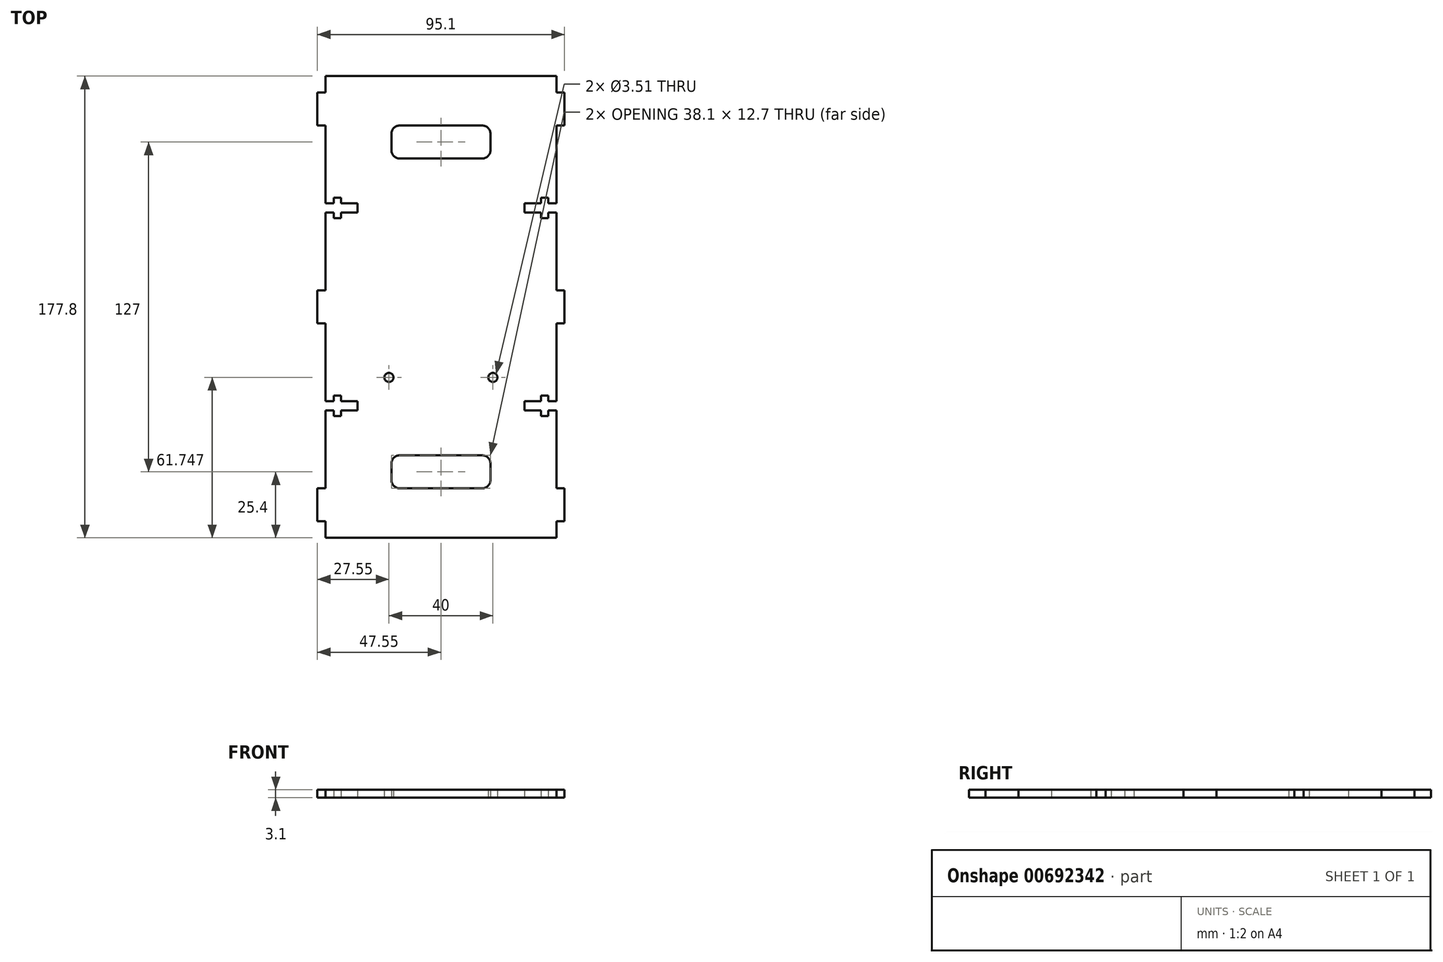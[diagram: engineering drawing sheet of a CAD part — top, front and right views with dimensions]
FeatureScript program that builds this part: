
annotation { "Feature Type Name" : "Feature", "Feature Type Description" : "" }
export const myFeature = defineFeature(function(context is Context, id is Id, definition is map)
    precondition{}
    {
        {
            var Q0;
            Q0=qCreatedBy(makeId("Top.planeOp"),FACE);
            var sketch = newSketch(context, id + "F0", { "sketchPlane" : qUnion([Q0])});
            skLineSegment(sketch, "E0.bottom", {"start": v(-44.45, 88.9) * mm, "end": v(44.45, 88.9) * mm});
            skLineSegment(sketch, "E0.top", {"start": v(-44.45, -88.9) * mm, "end": v(44.45, -88.9) * mm});
            skLineSegment(sketch, "E0.left", {"start": v(-44.45, 88.9) * mm, "end": v(-44.45, 82.55) * mm});
            skLineSegment(sketch, "E0.right", {"start": v(44.45, 88.9) * mm, "end": v(44.45, 82.55) * mm});
            skPoint(sketch, "E0.middle", {"position": v(0, 0) * mm});
            skCircle(sketch, "E1", {"center": v(-20, -27.15) * mm, "radius": 1.75 * mm});
            skCircle(sketch, "E2.MirrorC", {"center": v(20, -27.15) * mm, "radius": 1.75 * mm});
            skLineSegment(sketch, "E3", {"start": v(-44.45, 38.1) * mm, "end": v(44.45, 38.1) * mm, "construction": true});
            skLineSegment(sketch, "E4.bottom", {"start": v(-44.45, 39.85) * mm, "end": v(-41.27, 39.85) * mm});
            skLineSegment(sketch, "E4.top", {"start": v(-44.45, 36.35) * mm, "end": v(-41.27, 36.35) * mm});
            skPoint(sketch, "E4.middle", {"position": v(-42.86, 38.1) * mm});
            skLineSegment(sketch, "E5.bottom", {"start": v(-41.27, 42.07) * mm, "end": v(-38.5, 42.07) * mm});
            skLineSegment(sketch, "E5.top", {"start": v(-41.27, 34.13) * mm, "end": v(-38.5, 34.13) * mm});
            skLineSegment(sketch, "E5.left", {"start": v(-41.28, 42.07) * mm, "end": v(-41.28, 39.85) * mm});
            skLineSegment(sketch, "E5.right", {"start": v(-38.5, 42.07) * mm, "end": v(-38.5, 39.85) * mm});
            skPoint(sketch, "E5.middle", {"position": v(-39.89, 38.1) * mm});
            skLineSegment(sketch, "E6.bottom", {"start": v(-38.5, 39.85) * mm, "end": v(-32.15, 39.85) * mm});
            skLineSegment(sketch, "E6.top", {"start": v(-38.5, 36.35) * mm, "end": v(-32.15, 36.35) * mm});
            skLineSegment(sketch, "E6.right", {"start": v(-32.15, 39.85) * mm, "end": v(-32.15, 36.35) * mm});
            skPoint(sketch, "E6.middle", {"position": v(-35.32, 38.1) * mm});
            skLineSegment(sketch, "E7.trimOffspring", {"start": v(-41.28, 36.35) * mm, "end": v(-41.28, 34.13) * mm});
            skLineSegment(sketch, "E8.trimOffspring", {"start": v(-38.5, 36.35) * mm, "end": v(-38.5, 34.13) * mm});
            skLineSegment(sketch, "E9.trimOffspring", {"start": v(-44.45, 36.35) * mm, "end": v(-44.45, 6.35) * mm});
            skLineSegment(sketch, "E10.MirrorCS", {"start": v(-38.5, -36.35) * mm, "end": v(-38.5, -34.13) * mm});
            skLineSegment(sketch, "E11.MirrorCS", {"start": v(-38.5, -39.85) * mm, "end": v(-32.15, -39.85) * mm});
            skLineSegment(sketch, "E12.MirrorCS", {"start": v(-41.27, -36.35) * mm, "end": v(-41.27, -34.13) * mm});
            skLineSegment(sketch, "E13.MirrorCS", {"start": v(-38.5, -42.07) * mm, "end": v(-38.5, -39.85) * mm});
            skLineSegment(sketch, "E14.MirrorCS", {"start": v(-41.27, -42.07) * mm, "end": v(-41.27, -39.85) * mm});
            skLineSegment(sketch, "E15.MirrorCS", {"start": v(-41.27, -34.13) * mm, "end": v(-38.5, -34.13) * mm});
            skLineSegment(sketch, "E16.MirrorCS", {"start": v(-41.27, -42.07) * mm, "end": v(-38.5, -42.07) * mm});
            skLineSegment(sketch, "E17.MirrorCS", {"start": v(-44.45, -39.85) * mm, "end": v(-41.27, -39.85) * mm});
            skLineSegment(sketch, "E18.MirrorCS", {"start": v(-44.45, -36.35) * mm, "end": v(-41.27, -36.35) * mm});
            skPoint(sketch, "E19.MirrorP", {"position": v(-42.86, -38.1) * mm});
            skLineSegment(sketch, "E20.MirrorCS", {"start": v(-44.45, -36.35) * mm, "end": v(-44.45, -6.35) * mm});
            skPoint(sketch, "E21.MirrorP", {"position": v(-35.32, -38.1) * mm});
            skLineSegment(sketch, "E22.MirrorCS", {"start": v(-38.5, -36.35) * mm, "end": v(-32.15, -36.35) * mm});
            skLineSegment(sketch, "E23.MirrorCS", {"start": v(-32.15, -39.85) * mm, "end": v(-32.15, -36.35) * mm});
            skPoint(sketch, "E24.MirrorP", {"position": v(-39.89, -38.1) * mm});
            skLineSegment(sketch, "E25.MirrorCS", {"start": v(-44.45, -88.9) * mm, "end": v(-44.45, -82.55) * mm});
            skLineSegment(sketch, "E26.MirrorCS", {"start": v(-44.45, -38.1) * mm, "end": v(44.45, -38.1) * mm, "construction": true});
            skLineSegment(sketch, "E27.trimOffspring", {"start": v(-44.45, -39.85) * mm, "end": v(-44.45, -69.85) * mm});
            skLineSegment(sketch, "E28.trimOffspring", {"start": v(-44.45, 39.85) * mm, "end": v(-44.45, 69.85) * mm});
            skLineSegment(sketch, "E29.MirrorCS", {"start": v(44.45, 36.35) * mm, "end": v(41.27, 36.35) * mm});
            skLineSegment(sketch, "E30.MirrorCS", {"start": v(44.45, 39.85) * mm, "end": v(41.27, 39.85) * mm});
            skLineSegment(sketch, "E31.MirrorCS", {"start": v(38.5, 36.35) * mm, "end": v(38.5, 34.13) * mm});
            skPoint(sketch, "E32.MirrorP", {"position": v(42.86, 38.1) * mm});
            skLineSegment(sketch, "E33.MirrorCS", {"start": v(44.45, -39.85) * mm, "end": v(41.27, -39.85) * mm});
            skLineSegment(sketch, "E34.MirrorCS", {"start": v(44.45, -36.35) * mm, "end": v(41.27, -36.35) * mm});
            skLineSegment(sketch, "E35.MirrorCS", {"start": v(38.5, 42.07) * mm, "end": v(38.5, 39.85) * mm});
            skLineSegment(sketch, "E36.MirrorCS", {"start": v(41.27, 42.07) * mm, "end": v(41.27, 39.85) * mm});
            skLineSegment(sketch, "E37.MirrorCS", {"start": v(41.27, 34.13) * mm, "end": v(38.5, 34.13) * mm});
            skLineSegment(sketch, "E38.MirrorCS", {"start": v(41.27, 36.35) * mm, "end": v(41.27, 34.13) * mm});
            skLineSegment(sketch, "E39.MirrorCS", {"start": v(41.27, 42.07) * mm, "end": v(38.5, 42.07) * mm});
            skLineSegment(sketch, "E40.MirrorCS", {"start": v(38.5, -42.07) * mm, "end": v(38.5, -39.85) * mm});
            skLineSegment(sketch, "E41.MirrorCS", {"start": v(41.27, -42.07) * mm, "end": v(38.5, -42.07) * mm});
            skPoint(sketch, "E42.MirrorP", {"position": v(39.89, 38.1) * mm});
            skPoint(sketch, "E43.MirrorP", {"position": v(42.86, -38.1) * mm});
            skLineSegment(sketch, "E44.MirrorCS", {"start": v(32.15, -39.85) * mm, "end": v(32.15, -36.35) * mm});
            skLineSegment(sketch, "E45.MirrorCS", {"start": v(41.27, -36.35) * mm, "end": v(41.27, -34.13) * mm});
            skLineSegment(sketch, "E46.MirrorCS", {"start": v(41.27, -34.13) * mm, "end": v(38.5, -34.13) * mm});
            skLineSegment(sketch, "E47.MirrorCS", {"start": v(32.15, 39.85) * mm, "end": v(32.15, 36.35) * mm});
            skLineSegment(sketch, "E48.MirrorCS", {"start": v(41.27, -42.07) * mm, "end": v(41.27, -39.85) * mm});
            skPoint(sketch, "E49.MirrorP", {"position": v(39.89, -38.1) * mm});
            skLineSegment(sketch, "E50.MirrorCS", {"start": v(38.5, -36.35) * mm, "end": v(38.5, -34.13) * mm});
            skLineSegment(sketch, "E51.MirrorCS", {"start": v(44.45, -39.85) * mm, "end": v(44.45, -69.85) * mm});
            skLineSegment(sketch, "E52.MirrorCS", {"start": v(44.45, -36.35) * mm, "end": v(44.45, -6.35) * mm});
            skLineSegment(sketch, "E53.MirrorCS", {"start": v(38.5, 36.35) * mm, "end": v(32.15, 36.35) * mm});
            skLineSegment(sketch, "E54.MirrorCS", {"start": v(38.5, -36.35) * mm, "end": v(32.15, -36.35) * mm});
            skLineSegment(sketch, "E55.MirrorCS", {"start": v(38.5, -39.85) * mm, "end": v(32.15, -39.85) * mm});
            skLineSegment(sketch, "E56.MirrorCS", {"start": v(38.5, 39.85) * mm, "end": v(32.15, 39.85) * mm});
            skPoint(sketch, "E57.MirrorP", {"position": v(35.32, -38.1) * mm});
            skLineSegment(sketch, "E58.MirrorCS", {"start": v(44.45, 36.35) * mm, "end": v(44.45, 6.35) * mm});
            skLineSegment(sketch, "E59.MirrorCS", {"start": v(44.45, -38.1) * mm, "end": v(-44.45, -38.1) * mm, "construction": true});
            skPoint(sketch, "E60.MirrorP", {"position": v(35.32, 38.1) * mm});
            skLineSegment(sketch, "E61.MirrorCS", {"start": v(44.45, 39.85) * mm, "end": v(44.45, 69.85) * mm});
            skLineSegment(sketch, "E62.MirrorCS", {"start": v(44.45, 38.1) * mm, "end": v(-44.45, 38.1) * mm, "construction": true});
            skLineSegment(sketch, "E63.bottom", {"start": v(-19.05, -69.85) * mm, "end": v(19.05, -69.85) * mm});
            skLineSegment(sketch, "E63.top", {"start": v(-19.05, -57.15) * mm, "end": v(19.05, -57.15) * mm});
            skLineSegment(sketch, "E63.left", {"start": v(-19.05, -69.85) * mm, "end": v(-19.05, -57.15) * mm});
            skLineSegment(sketch, "E63.right", {"start": v(19.05, -69.85) * mm, "end": v(19.05, -57.15) * mm});
            skPoint(sketch, "E63.middle", {"position": v(0, -63.5) * mm});
            skPoint(sketch, "E64.MirrorP", {"position": v(0, 63.5) * mm});
            skLineSegment(sketch, "E65.MirrorCS", {"start": v(-19.05, 69.85) * mm, "end": v(19.05, 69.85) * mm});
            skLineSegment(sketch, "E66.MirrorCS", {"start": v(-19.05, 57.15) * mm, "end": v(19.05, 57.15) * mm});
            skLineSegment(sketch, "E67.MirrorCS", {"start": v(-19.05, 69.85) * mm, "end": v(-19.05, 57.15) * mm});
            skLineSegment(sketch, "E68.MirrorCS", {"start": v(19.05, 69.85) * mm, "end": v(19.05, 57.15) * mm});
            skLineSegment(sketch, "E69.bottom", {"start": v(-44.45, 6.35) * mm, "end": v(-47.55, 6.35) * mm});
            skLineSegment(sketch, "E69.top", {"start": v(-44.45, -6.35) * mm, "end": v(-47.55, -6.35) * mm});
            skLineSegment(sketch, "E69.right", {"start": v(-47.55, 6.35) * mm, "end": v(-47.55, -6.35) * mm});
            skPoint(sketch, "E69.middle", {"position": v(-46, 0) * mm});
            skLineSegment(sketch, "E70.bottom", {"start": v(-44.45, 82.55) * mm, "end": v(-47.55, 82.55) * mm});
            skLineSegment(sketch, "E70.top", {"start": v(-44.45, 69.85) * mm, "end": v(-47.55, 69.85) * mm});
            skLineSegment(sketch, "E70.right", {"start": v(-47.55, 82.55) * mm, "end": v(-47.55, 69.85) * mm});
            skPoint(sketch, "E70.middle", {"position": v(-46, 76.2) * mm});
            skLineSegment(sketch, "E71.trimOffspring", {"start": v(-44.45, -6.35) * mm, "end": v(-44.45, -36.35) * mm});
            skLineSegment(sketch, "E72.trimOffspring", {"start": v(-44.45, 6.35) * mm, "end": v(-44.45, 36.35) * mm});
            skLineSegment(sketch, "E73.trimOffspring", {"start": v(-44.45, 82.55) * mm, "end": v(-44.45, 88.9) * mm});
            skLineSegment(sketch, "E74.trimOffspring", {"start": v(-44.45, 69.85) * mm, "end": v(-44.45, 39.85) * mm});
            skLineSegment(sketch, "E75.MirrorCS", {"start": v(-44.45, -82.55) * mm, "end": v(-47.55, -82.55) * mm});
            skLineSegment(sketch, "E76.MirrorCS", {"start": v(-44.45, -69.85) * mm, "end": v(-47.55, -69.85) * mm});
            skLineSegment(sketch, "E77.MirrorCS", {"start": v(-47.55, -82.55) * mm, "end": v(-47.55, -69.85) * mm});
            skPoint(sketch, "E78.MirrorP", {"position": v(-46, -76.2) * mm});
            skLineSegment(sketch, "E79.trimOffspring", {"start": v(-44.45, -82.55) * mm, "end": v(-44.45, -88.9) * mm});
            skLineSegment(sketch, "E80.trimOffspring", {"start": v(-44.45, -69.85) * mm, "end": v(-44.45, -39.85) * mm});
            skLineSegment(sketch, "E81.MirrorCS", {"start": v(47.55, 82.55) * mm, "end": v(47.55, 69.85) * mm});
            skPoint(sketch, "E82.MirrorP", {"position": v(46, 76.2) * mm});
            skLineSegment(sketch, "E83.MirrorCS", {"start": v(44.45, 82.55) * mm, "end": v(47.55, 82.55) * mm});
            skLineSegment(sketch, "E84.MirrorCS", {"start": v(44.45, 69.85) * mm, "end": v(47.55, 69.85) * mm});
            skLineSegment(sketch, "E85.MirrorCS", {"start": v(44.45, -6.35) * mm, "end": v(47.55, -6.35) * mm});
            skLineSegment(sketch, "E86.MirrorCS", {"start": v(47.55, 6.35) * mm, "end": v(47.55, -6.35) * mm});
            skLineSegment(sketch, "E87.MirrorCS", {"start": v(44.45, 6.35) * mm, "end": v(47.55, 6.35) * mm});
            skPoint(sketch, "E88.MirrorP", {"position": v(46, 0) * mm});
            skLineSegment(sketch, "E89.MirrorCS", {"start": v(44.45, -82.55) * mm, "end": v(47.55, -82.55) * mm});
            skLineSegment(sketch, "E90.MirrorCS", {"start": v(44.45, -69.85) * mm, "end": v(47.55, -69.85) * mm});
            skLineSegment(sketch, "E91.MirrorCS", {"start": v(47.55, -82.55) * mm, "end": v(47.55, -69.85) * mm});
            skPoint(sketch, "E92.MirrorP", {"position": v(46, -76.2) * mm});
            skLineSegment(sketch, "E93.trimOffspring", {"start": v(44.45, -82.55) * mm, "end": v(44.45, -88.9) * mm});
            skLineSegment(sketch, "E94.trimOffspring", {"start": v(44.45, -6.35) * mm, "end": v(44.45, -36.35) * mm});
            skLineSegment(sketch, "E95.trimOffspring", {"start": v(44.45, 6.35) * mm, "end": v(44.45, 36.35) * mm});
            skLineSegment(sketch, "E96.trimOffspring", {"start": v(44.45, -69.85) * mm, "end": v(44.45, -39.85) * mm});
            skPoint(sketch, "E97.MirrorCS.start.orphan", {"position": v(44.45, -88.9) * mm});
            skLineSegment(sketch, "E98.trimOffspring", {"start": v(44.45, 69.85) * mm, "end": v(44.45, 39.85) * mm});
            skLineSegment(sketch, "E99.trimOffspring", {"start": v(44.45, 82.55) * mm, "end": v(44.45, 88.9) * mm});
            skSolve(sketch);
        }
        {
            var Q0;
            Q0 = qSketchRegion(id + "F0", true);
            extrude(context, id + "F1", {"entities" : qUnion([Q0]), "depth" : 3.1 * mm, "offsetDistance" : 25.4 * mm});
        }
        {
            var Q0;
            Q0=makeQuery(id+"F1.opExtrude","SWEPT_EDGE",EDGE,{"disambiguationData":[OSD([sQuery(id+"F0.wireOp",EDGE,"E66.MirrorCS"),sQuery(id+"F0.wireOp",EDGE,"E68.MirrorCS")])]});
            var Q1;
            Q1=makeQuery(id+"F1.opExtrude","SWEPT_EDGE",EDGE,{"disambiguationData":[OSD([sQuery(id+"F0.wireOp",EDGE,"E63.bottom"),sQuery(id+"F0.wireOp",EDGE,"E63.right")])]});
            var Q2;
            Q2=makeQuery(id+"F1.opExtrude","SWEPT_EDGE",EDGE,{"disambiguationData":[OSD([sQuery(id+"F0.wireOp",EDGE,"E66.MirrorCS"),sQuery(id+"F0.wireOp",EDGE,"E67.MirrorCS")])]});
            var Q3;
            Q3=makeQuery(id+"F1.opExtrude","SWEPT_EDGE",EDGE,{"disambiguationData":[OSD([sQuery(id+"F0.wireOp",EDGE,"E63.bottom"),sQuery(id+"F0.wireOp",EDGE,"E63.left")])]});
            var Q4;
            Q4=makeQuery(id+"F1.opExtrude","SWEPT_EDGE",EDGE,{"disambiguationData":[OSD([sQuery(id+"F0.wireOp",EDGE,"E65.MirrorCS"),sQuery(id+"F0.wireOp",EDGE,"E68.MirrorCS")])]});
            var Q5;
            Q5=makeQuery(id+"F1.opExtrude","SWEPT_EDGE",EDGE,{"disambiguationData":[OSD([sQuery(id+"F0.wireOp",EDGE,"E63.top"),sQuery(id+"F0.wireOp",EDGE,"E63.right")])]});
            var Q6;
            Q6=makeQuery(id+"F1.opExtrude","SWEPT_EDGE",EDGE,{"disambiguationData":[OSD([sQuery(id+"F0.wireOp",EDGE,"E63.top"),sQuery(id+"F0.wireOp",EDGE,"E63.left")])]});
            var Q7;
            Q7=makeQuery(id+"F1.opExtrude","SWEPT_EDGE",EDGE,{"disambiguationData":[OSD([sQuery(id+"F0.wireOp",EDGE,"E65.MirrorCS"),sQuery(id+"F0.wireOp",EDGE,"E67.MirrorCS")])]});
            fillet(context, id + "F2", {"entities" : qUnion([Q0, Q1, Q2, Q3, Q4, Q5, Q6, Q7]), "radius" : 3.17 * mm, "tangentPropagation" : true, "allowEdgeOverflow" : false});
        }
    });
